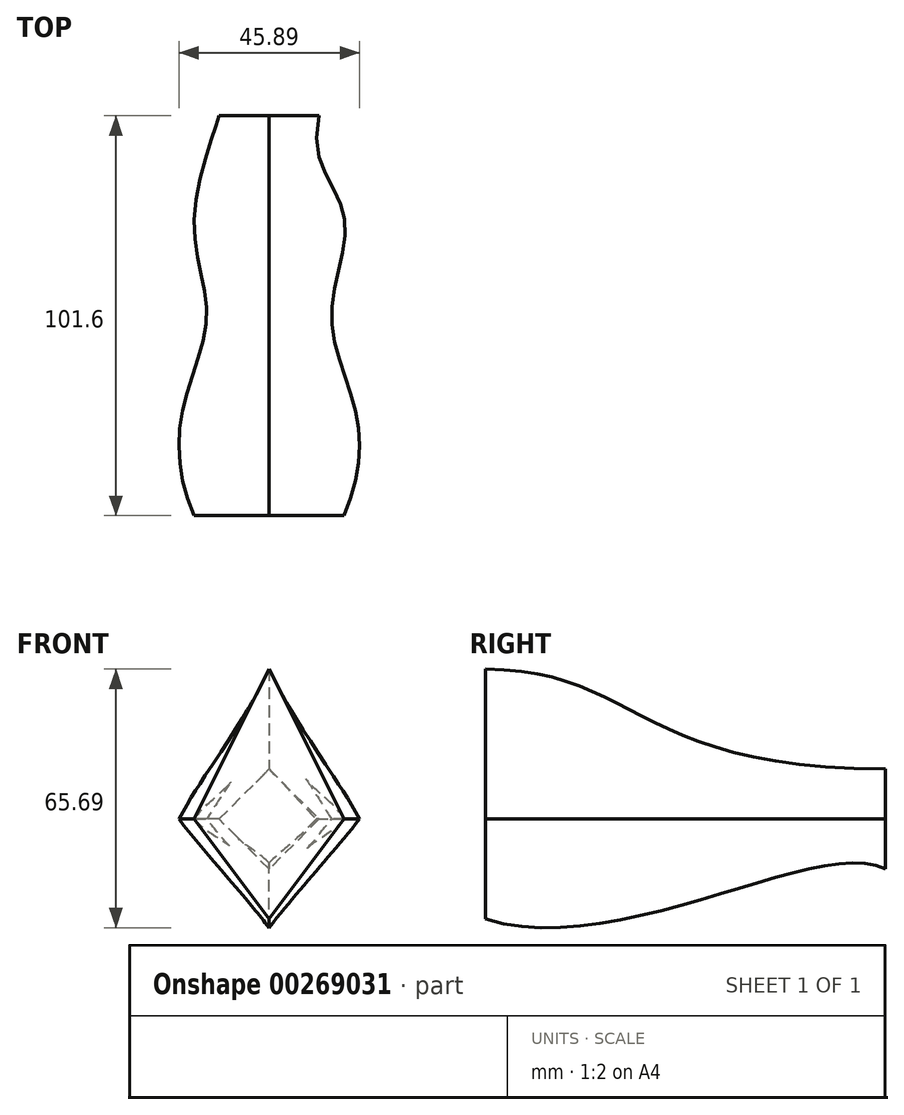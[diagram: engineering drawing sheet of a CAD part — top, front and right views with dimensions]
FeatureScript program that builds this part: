
annotation { "Feature Type Name" : "Feature", "Feature Type Description" : "" }
export const myFeature = defineFeature(function(context is Context, id is Id, definition is map)
    precondition{}
    {
        {
            var Q0;
            Q0=qCreatedBy(makeId("Top.planeOp"),FACE);
            var sketch = newSketch(context, id + "F0", { "sketchPlane" : qUnion([Q0])});
            skLineSegment(sketch, "E0", {"start": v(-12.7, 50.8) * mm, "end": v(12.7, 50.8) * mm});
            skLineSegment(sketch, "E1", {"start": v(-19.05, 25.4) * mm, "end": v(19.05, 25.4) * mm});
            skLineSegment(sketch, "E2", {"start": v(-15.88, 0) * mm, "end": v(15.88, 0) * mm});
            skLineSegment(sketch, "E3", {"start": v(-22.22, -25.4) * mm, "end": v(22.23, -25.4) * mm});
            skLineSegment(sketch, "E4", {"start": v(-19.05, -50.8) * mm, "end": v(19.05, -50.8) * mm});
            skLineSegment(sketch, "E5", {"start": v(0, 50.8) * mm, "end": v(0, -50.8) * mm});
            skFitSpline(sketch, "E6", {"points": [v(-12.7, 50.8) * mm, v(-19.05, 25.4) * mm, v(-15.88, 0) * mm, v(-22.22, -25.4) * mm, v(-19.05, -50.8) * mm], "startDerivative": vector(-10.34, -41.06) * mm, "endDerivative": vector(43.54, -101.6) * mm});
            skFitSpline(sketch, "E7", {"points": [v(12.7, 50.8) * mm, v(19.05, 25.4) * mm, v(15.88, 0) * mm, v(22.23, -25.4) * mm, v(19.05, -50.8) * mm], "startDerivative": vector(-37.03, -141.36) * mm, "endDerivative": vector(-43.54, -101.6) * mm});
            skSolve(sketch);
        }
        {
            var Q0;
            Q0=qCreatedBy(makeId("Top.planeOp"),FACE);
            var sketch = newSketch(context, id + "F1", { "sketchPlane" : qUnion([Q0])});
            skFitSpline(sketch, "E8", {"points": [v(-12.7, 50.8) * mm, v(-19.05, 25.4) * mm, v(-15.88, 0) * mm, v(-22.22, -25.4) * mm, v(-19.05, -50.8) * mm], "startDerivative": vector(-49.2, -60.6) * mm, "endDerivative": vector(49.83, -102.8) * mm});
            skSolve(sketch);
        }
        {
            var Q0;
            Q0=qCreatedBy(makeId("Right.planeOp"),FACE);
            var sketch = newSketch(context, id + "F2", { "sketchPlane" : qUnion([Q0])});
            skLineSegment(sketch, "E9", {"start": v(50.8, 12.7) * mm, "end": v(50.8, -12.7) * mm});
            skLineSegment(sketch, "E10", {"start": v(25.4, 14.35) * mm, "end": v(25.4, -14.16) * mm});
            skLineSegment(sketch, "E11", {"start": v(0, 21.05) * mm, "end": v(0, -21.56) * mm});
            skLineSegment(sketch, "E12", {"start": v(-25.4, 33.19) * mm, "end": v(-25.4, -26.99) * mm});
            skLineSegment(sketch, "E13", {"start": v(-50.8, 38.1) * mm, "end": v(-50.8, -25.4) * mm});
            skLineSegment(sketch, "E14", {"start": v(-50.8, -25.4) * mm, "end": v(-63.5, -25.4) * mm, "construction": true});
            skLineSegment(sketch, "E15", {"start": v(-50.8, 38.1) * mm, "end": v(-63.5, 38.1) * mm, "construction": true});
            skFitSpline(sketch, "E16", {"points": [v(-50.8, 38.1) * mm, v(50.8, 12.7) * mm], "startDerivative": vector(114.3, 0) * mm, "endDerivative": vector(190.5, 0) * mm});
            skFitSpline(sketch, "E17", {"points": [v(-50.8, -25.4) * mm, v(50.8, -12.7) * mm], "startDerivative": vector(102.59, -31.97) * mm, "endDerivative": vector(51.92, -26.5) * mm});
            skSolve(sketch);
        }
        {
            var Q0;
            Q0=qCreatedBy(makeId("Front.planeOp"),FACE);
            var Q1;
            Q1=sQuery(id+"F0.wireOp",VERTEX,"E5.start");
            cPlane(context, id + "F3", {"entities" : qUnion([Q0, Q1]), "cplaneType" : CPlaneType.PLANE_POINT, "offset" : 25.4 * mm, "width" : 152.4 * mm, "height" : 152.4 * mm});
        }
        {
            var Q0;
            Q0=sQuery(id+"F0.wireOp",EDGE,"E1");
            cPoint(context, id + "F4", {"entities" : qUnion([Q0]), "parameter" : 0.5});
        }
        {
            var Q0;
            Q0=qCreatedBy(makeId("Front.planeOp"),FACE);
            var Q1;
            Q1 = qCreatedBy(id + "F4" ,VERTEX);
            cPlane(context, id + "F5", {"entities" : qUnion([Q0, Q1]), "cplaneType" : CPlaneType.PLANE_POINT, "offset" : 25.4 * mm, "width" : 152.4 * mm, "height" : 152.4 * mm});
        }
        {
            var Q0;
            Q0=sQuery(id+"F0.wireOp",EDGE,"E2");
            cPoint(context, id + "F6", {"entities" : qUnion([Q0]), "parameter" : 0.5});
        }
        {
            var Q0;
            Q0=qCreatedBy(makeId("Front.planeOp"),FACE);
            var Q1;
            Q1 = qCreatedBy(id + "F6" ,VERTEX);
            cPlane(context, id + "F7", {"entities" : qUnion([Q0, Q1]), "cplaneType" : CPlaneType.PLANE_POINT, "offset" : 25.4 * mm, "width" : 152.4 * mm, "height" : 152.4 * mm});
        }
        {
            var Q0;
            Q0=sQuery(id+"F0.wireOp",EDGE,"E3");
            cPoint(context, id + "F8", {"entities" : qUnion([Q0]), "parameter" : 0.5});
        }
        {
            var Q0;
            Q0=qCreatedBy(makeId("Front.planeOp"),FACE);
            var Q1;
            Q1 = qCreatedBy(id + "F8" ,VERTEX);
            cPlane(context, id + "F9", {"entities" : qUnion([Q0, Q1]), "cplaneType" : CPlaneType.PLANE_POINT, "offset" : 25.4 * mm, "width" : 152.4 * mm, "height" : 152.4 * mm});
        }
        {
            var Q0;
            Q0=sQuery(id+"F0.wireOp",EDGE,"E4");
            cPoint(context, id + "F10", {"entities" : qUnion([Q0]), "parameter" : 0.5});
        }
        {
            var Q0;
            Q0=qCreatedBy(makeId("Front.planeOp"),FACE);
            var Q1;
            Q1 = qCreatedBy(id + "F10" ,VERTEX);
            cPlane(context, id + "F11", {"entities" : qUnion([Q0, Q1]), "cplaneType" : CPlaneType.PLANE_POINT, "offset" : 25.4 * mm, "width" : 152.4 * mm, "height" : 152.4 * mm});
        }
        {
            var Q0;
            Q0=qCreatedBy(id+"F3.planeOp",FACE);
            var sketch = newSketch(context, id + "F12", { "sketchPlane" : qUnion([Q0])});
            skLineSegment(sketch, "E18", {"start": v(0, 12.7) * mm, "end": v(12.7, 0) * mm});
            skLineSegment(sketch, "E19", {"start": v(12.7, 0) * mm, "end": v(0, -12.7) * mm});
            skLineSegment(sketch, "E20", {"start": v(0, -12.7) * mm, "end": v(-12.7, 0) * mm});
            skLineSegment(sketch, "E21", {"start": v(-12.7, 0) * mm, "end": v(0, 12.7) * mm});
            skSolve(sketch);
        }
        {
            var Q0;
            Q0=qCreatedBy(id+"F11.planeOp",FACE);
            var sketch = newSketch(context, id + "F13", { "sketchPlane" : qUnion([Q0])});
            skLineSegment(sketch, "E22", {"start": v(0, 38.1) * mm, "end": v(19.05, 0) * mm});
            skLineSegment(sketch, "E23", {"start": v(19.05, 0) * mm, "end": v(0, -25.4) * mm});
            skLineSegment(sketch, "E24", {"start": v(0, -25.4) * mm, "end": v(-19.05, 0) * mm});
            skLineSegment(sketch, "E25", {"start": v(-19.05, 0) * mm, "end": v(0, 38.1) * mm});
            skSolve(sketch);
        }
        {
            var Q0;
            Q0=makeQuery(id+"F12.imprint","IMPRINT",FACE,{"disambiguationData":[TD([[makeQuery(id+"F12.imprint","IMPRINT",EDGE,{"derivedFrom":sQuery(id+"F12.wireOp",EDGE,"E18")}),-1.0]])]});
            var Q1;
            Q1=makeQuery(id+"F13.imprint","IMPRINT",FACE,{"disambiguationData":[TD([[makeQuery(id+"F13.imprint","IMPRINT",EDGE,{"derivedFrom":sQuery(id+"F13.wireOp",EDGE,"E22")}),-1.0]])]});
            var Q2;
            Q2=sQuery(id+"F2.wireOp",EDGE,"E16");
            var Q3;
            Q3=sQuery(id+"F2.wireOp",EDGE,"E17");
            var Q4;
            Q4=sQuery(id+"F0.wireOp",EDGE,"E6");
            var Q5;
            Q5=sQuery(id+"F0.wireOp",EDGE,"E7");
            loft(context, id + "F14", {"addGuides" : true, "sheetProfilesArray" : [{ "sheetProfileEntities" : qUnion([Q0]) }, { "sheetProfileEntities" : qUnion([Q1]) }], "guidesArray" : [{ "guideEntities" : qUnion([Q2]), "guideDerivativeType" : LoftGuideDerivativeType.DEFAULT, "guideDerivativeMagnitude" : 1 }, { "guideEntities" : qUnion([Q3]), "guideDerivativeType" : LoftGuideDerivativeType.DEFAULT, "guideDerivativeMagnitude" : 1 }, { "guideEntities" : qUnion([Q4]), "guideDerivativeType" : LoftGuideDerivativeType.DEFAULT, "guideDerivativeMagnitude" : 1 }, { "guideEntities" : qUnion([Q5]), "guideDerivativeType" : LoftGuideDerivativeType.DEFAULT, "guideDerivativeMagnitude" : 1 }]});
        }
    });
